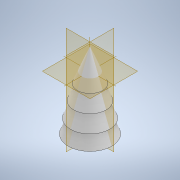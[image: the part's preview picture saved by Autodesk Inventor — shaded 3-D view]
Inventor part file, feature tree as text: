
AUTODESK INVENTOR PART (.ipt)
format: ipt  version: 2022.4 (Build 264492010, 492A)  size: 144,384 bytes
history: native  units: mm
features: revolve x1, sketch x1
ambient origin geometry x8: Origin, YZ Plane, XZ Plane, XY Plane, X Axis, Y Axis, Z Axis, Center Point
bodies: Body1 (feature_tree)
feature tree (2):
  revolve  "Revolution2"  [1 undecoded]
  sketch  "Sketch1"  dims[d0=70.0mm d1=40.0mm d2=20.0mm d3=5.0mm d4=10.0mm d5=5.0mm d6=5.0mm d8=15.0mm d9=15.0mm d10=360.0deg]
note: 1 required parameter value undecoded (feature->parameter linkage not recoverable at this tier; creation-order binding heuristic only, values carry confidence <= 0.55)
